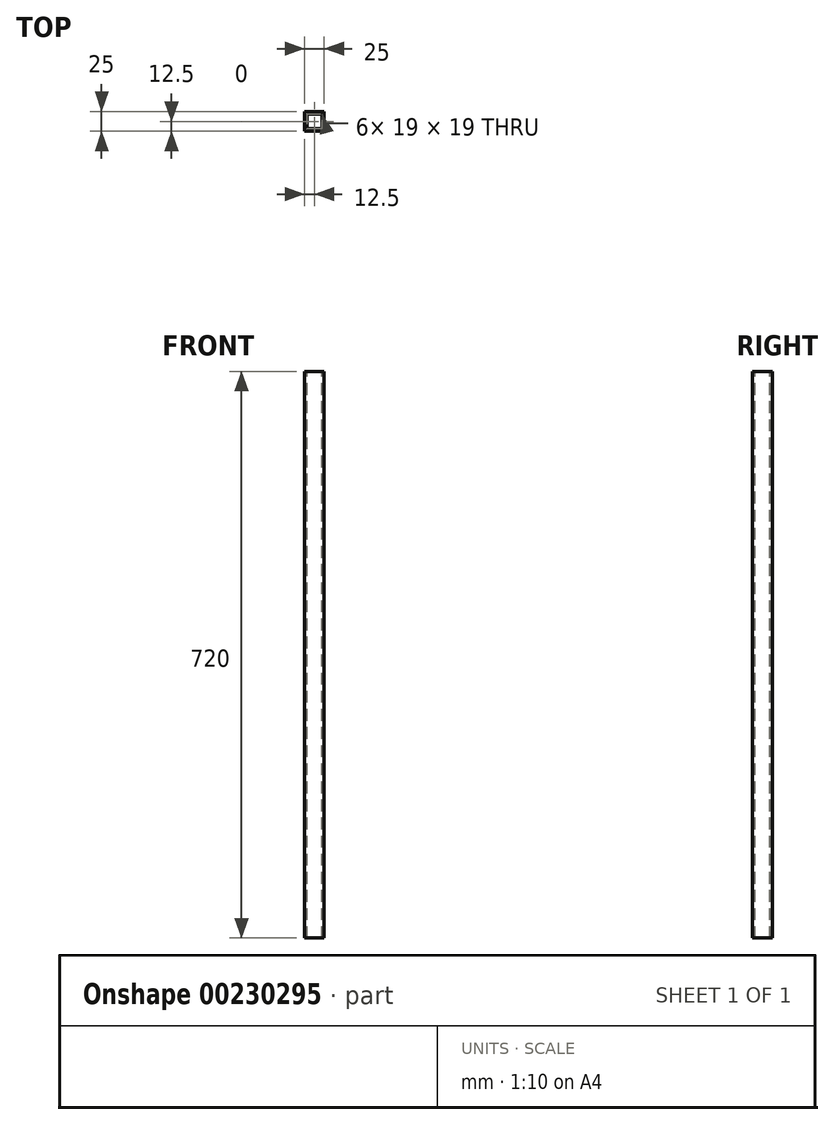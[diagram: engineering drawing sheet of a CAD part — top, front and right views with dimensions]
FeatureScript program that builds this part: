
annotation { "Feature Type Name" : "Feature", "Feature Type Description" : "" }
export const myFeature = defineFeature(function(context is Context, id is Id, definition is map)
    precondition{}
    {
        {
            var Q0;
            Q0=qCreatedBy(makeId("Top.planeOp"),FACE);
            var sketch = newSketch(context, id + "F0", { "sketchPlane" : qUnion([Q0])});
            skLineSegment(sketch, "E0.bottom", {"start": v(0, 0) * mm, "end": v(25, 0) * mm});
            skLineSegment(sketch, "E0.top", {"start": v(0, -25) * mm, "end": v(25, -25) * mm});
            skLineSegment(sketch, "E0.left", {"start": v(0, 0) * mm, "end": v(0, -25) * mm});
            skLineSegment(sketch, "E0.right", {"start": v(25, 0) * mm, "end": v(25, -25) * mm});
            skLineSegment(sketch, "E1.bottom", {"start": v(3, -3) * mm, "end": v(22, -3) * mm});
            skLineSegment(sketch, "E1.top", {"start": v(3, -22) * mm, "end": v(22, -22) * mm});
            skLineSegment(sketch, "E1.left", {"start": v(3, -3) * mm, "end": v(3, -22) * mm});
            skLineSegment(sketch, "E1.right", {"start": v(22, -3) * mm, "end": v(22, -22) * mm});
            skSolve(sketch);
        }
        {
            var Q0;
            Q0=makeQuery(id+"F0.imprint","IMPRINT",FACE,{"disambiguationData":[TD([[makeQuery(id+"F0.imprint","IMPRINT",EDGE,{"derivedFrom":sQuery(id+"F0.wireOp",EDGE,"E0.bottom")}),-1.0]])]});
            extrude(context, id + "F1", {"entities" : qUnion([Q0]), "oppositeDirection" : true, "depth" : 720 * mm});
        }
    });
